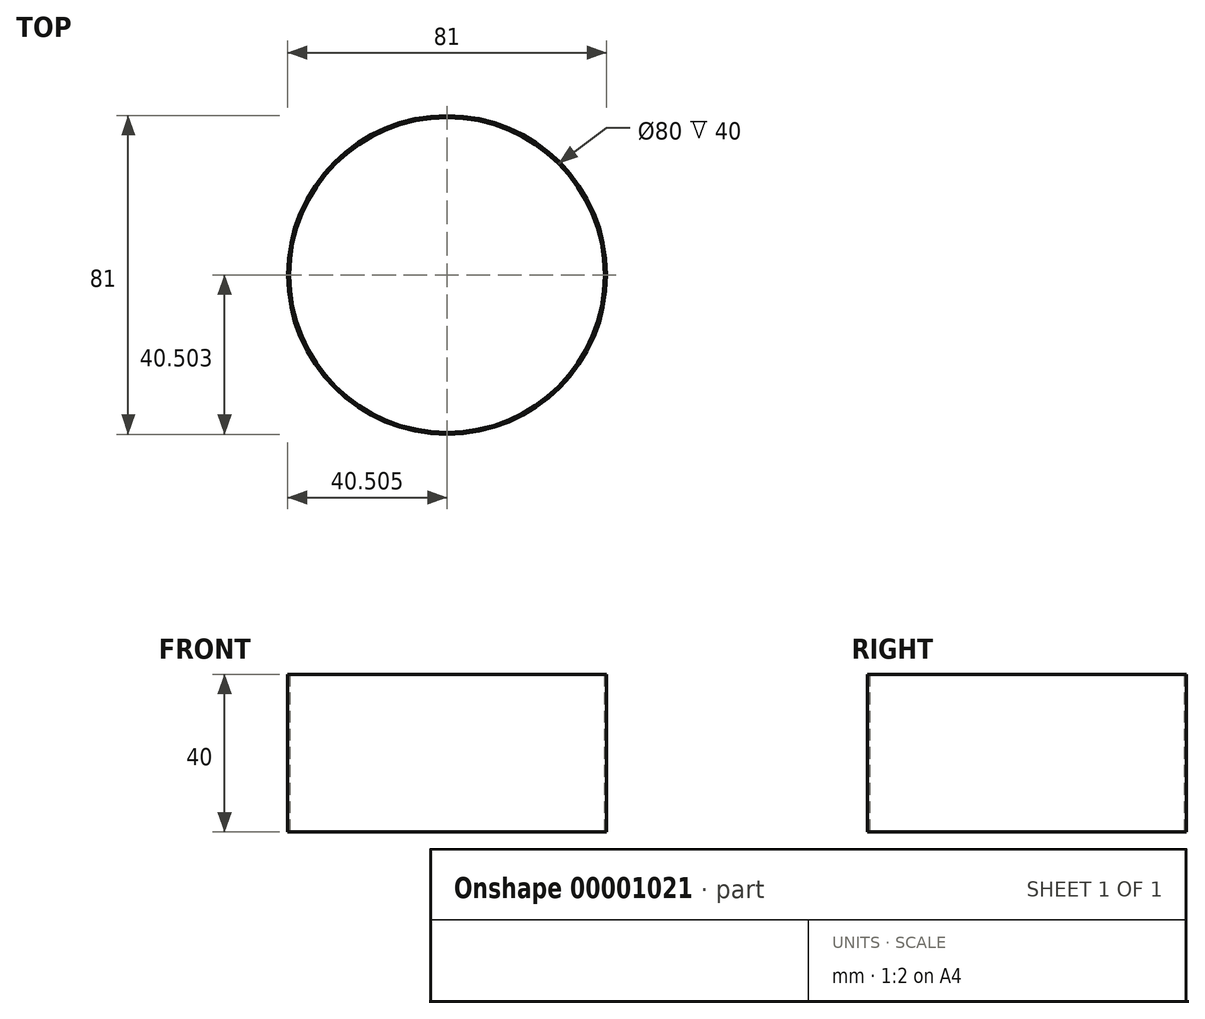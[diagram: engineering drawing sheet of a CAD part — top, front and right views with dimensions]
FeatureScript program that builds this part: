
annotation { "Feature Type Name" : "Feature", "Feature Type Description" : "" }
export const myFeature = defineFeature(function(context is Context, id is Id, definition is map)
    precondition{}
    {
        {
            var Q0;
            Q0=qCreatedBy(makeId("Top.planeOp"),FACE);
            var sketch = newSketch(context, id + "F0", { "sketchPlane" : qUnion([Q0])});
            skCircle(sketch, "E0", {"center": v(-3.75, 2.9) * mm, "radius": 40 * mm});
            skCircle(sketch, "E1", {"center": v(-3.75, 2.9) * mm, "radius": 40.5 * mm});
            skSolve(sketch);
        }
        {
            var Q0;
            Q0=makeQuery(id+"F0.imprint","IMPRINT",FACE,{"disambiguationData":[TD([[makeQuery(id+"F0.imprint","IMPRINT",EDGE,{"derivedFrom":sQuery(id+"F0.wireOp",EDGE,"E0")}),-1.0]])]});
            extrude(context, id + "F1", {"entities" : qUnion([Q0]), "depth" : 40 * mm});
        }
    });
